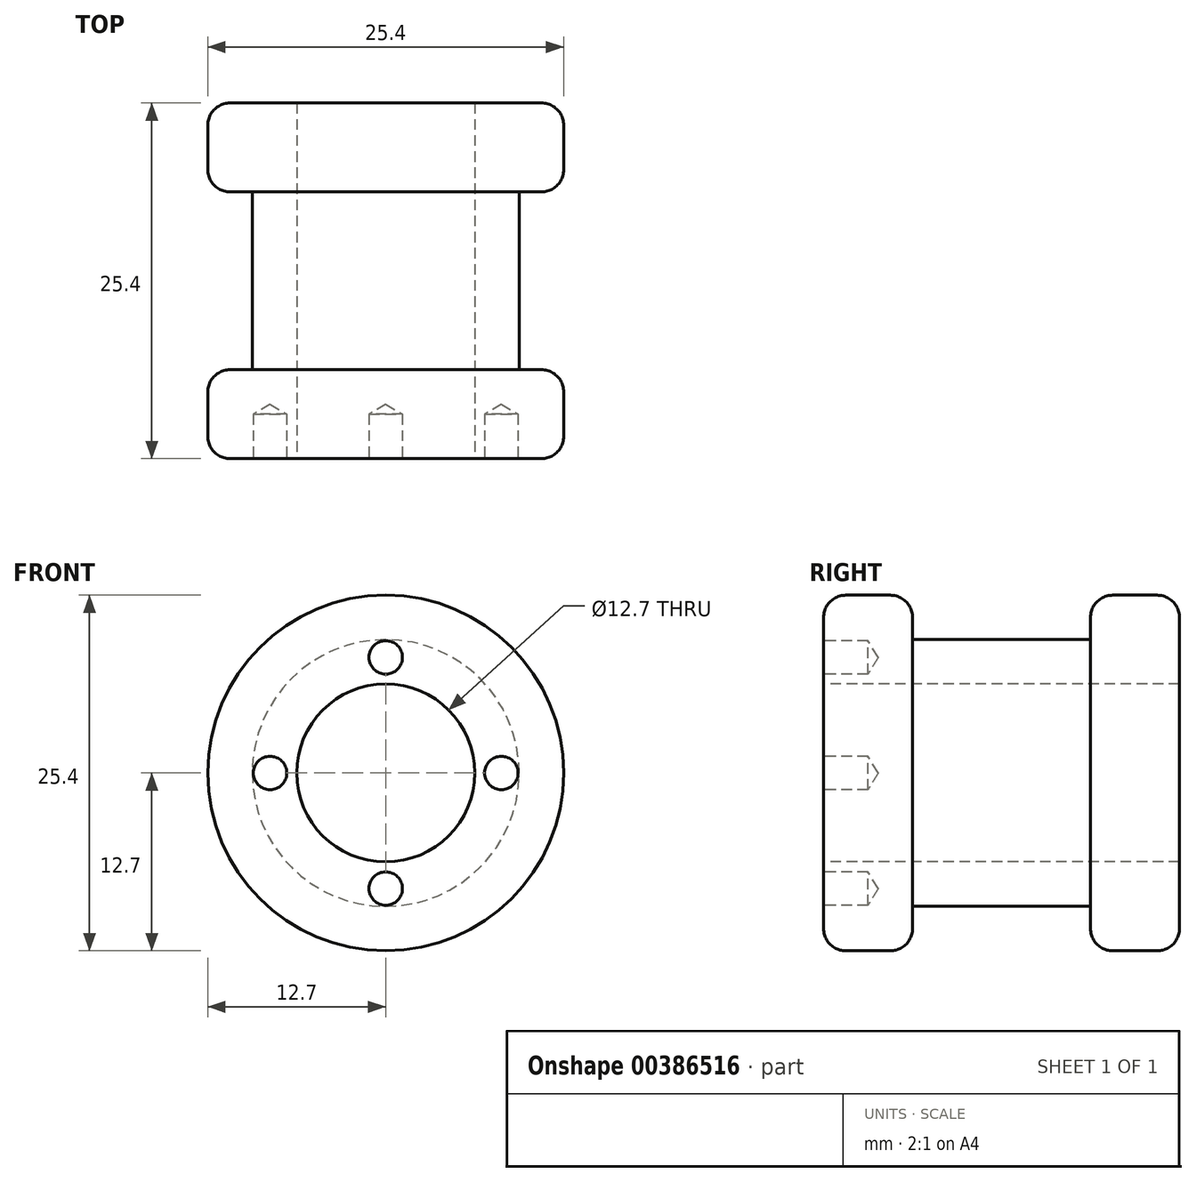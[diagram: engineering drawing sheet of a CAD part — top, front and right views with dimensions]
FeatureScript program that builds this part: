
annotation { "Feature Type Name" : "Feature", "Feature Type Description" : "" }
export const myFeature = defineFeature(function(context is Context, id is Id, definition is map)
    precondition{}
    {
        {
            var Q0;
            Q0=qCreatedBy(makeId("Front.planeOp"),FACE);
            var sketch = newSketch(context, id + "F0", { "sketchPlane" : qUnion([Q0])});
            skCircle(sketch, "E0", {"center": v(0, 0) * mm, "radius": 12.7 * mm});
            skSolve(sketch);
        }
        {
            var Q0;
            Q0=makeQuery(id+"F0.imprint","IMPRINT",FACE,{"disambiguationData":[TD([[makeQuery(id+"F0.imprint","IMPRINT",EDGE,{"derivedFrom":sQuery(id+"F0.wireOp",EDGE,"E0")}),1.0]])]});
            extrude(context, id + "F1", {"entities" : qUnion([Q0]), "depth" : 6.35 * mm});
        }
        {
            var Q0;
            Q0=makeQuery(id+"F1.opExtrude","CAP_FACE",FACE,{"disambiguationData":[OSD([sQuery(id+"F0.wireOp",EDGE,"E0")])],"isStart":false});
            var sketch = newSketch(context, id + "F2", { "sketchPlane" : qUnion([Q0])});
            skCircle(sketch, "E1", {"center": v(0, 0) * mm, "radius": 9.52 * mm});
            skSolve(sketch);
        }
        {
            var Q0;
            Q0=makeQuery(id+"F2.imprint","IMPRINT",FACE,{"disambiguationData":[TD([[makeQuery(id+"F2.imprint","IMPRINT",EDGE,{"derivedFrom":sQuery(id+"F2.wireOp",EDGE,"E1")}),1.0]])]});
            extrude(context, id + "F3", {"entities" : qUnion([Q0]), "operationType" : NewBodyOperationType.ADD, "depth" : 12.7 * mm});
        }
        {
            var Q0;
            Q0=makeQuery(id+"F3.opExtrude","CAP_FACE",FACE,{"disambiguationData":[OSD([sQuery(id+"F2.wireOp",EDGE,"E1")])],"isStart":false});
            var sketch = newSketch(context, id + "F4", { "sketchPlane" : qUnion([Q0])});
            skCircle(sketch, "E2", {"center": v(0, 0) * mm, "radius": 12.7 * mm});
            skSolve(sketch);
        }
        {
            var Q0;
            Q0=makeQuery(id+"F4.imprint","IMPRINT",FACE,{"disambiguationData":[TD([[makeQuery(id+"F4.imprint","IMPRINT",EDGE,{"derivedFrom":sQuery(id+"F4.wireOp",EDGE,"E2")}),1.0]])]});
            var Q1;
            Q1=makeQuery(id+"F4.imprint","IMPRINT",FACE,{"disambiguationData":[TD([[makeQuery(id+"F4.imprint","IMPRINT",EDGE,{"derivedFrom":makeQuery(id+"F3.opExtrude","CAP_EDGE",EDGE,{"disambiguationData":[OSD([sQuery(id+"F2.wireOp",EDGE,"E1")])],"isStart":false})}),1.0]])]});
            extrude(context, id + "F5", {"entities" : qUnion([Q0, Q1]), "operationType" : NewBodyOperationType.ADD, "depth" : 6.35 * mm});
        }
        {
            var Q0;
            Q0=makeQuery(id+"F5.opExtrude","CAP_FACE",FACE,{"disambiguationData":[OSD([sQuery(id+"F4.wireOp",EDGE,"E2")])],"isStart":false});
            var sketch = newSketch(context, id + "F6", { "sketchPlane" : qUnion([Q0])});
            skPoint(sketch, "E3", {"position": v(0, 8.26) * mm});
            skPoint(sketch, "E4", {"position": v(8.26, 0) * mm});
            skPoint(sketch, "E5", {"position": v(0, -8.26) * mm});
            skPoint(sketch, "E6", {"position": v(-8.26, 0) * mm});
            skPoint(sketch, "E7", {"position": v(0, 0) * mm});
            skSolve(sketch);
        }
        {
            var Q0;
            Q0=sQuery(id+"F6.wireOp",VERTEX,"E7");
            var Q1;
            Q1=makeQuery(id+"F1.opExtrude","SWEPT_BODY",BODY,{"disambiguationData":[OSD([sQuery(id+"F0.wireOp",EDGE,"E0")])]});
            hole(context, id + "F7", {"style" : HoleStyle.SIMPLE, "endStyle" : HoleEndStyle.THROUGH, "holeDiameter" : 12.7 * mm, "isTappedThrough" : true, "tappedDepth" : 12.7 * mm, "tapClearance" : 3, "locations" : qUnion([Q0]), "scope" : qUnion([Q1])});
        }
        {
            var Q0;
            Q0=sQuery(id+"F6.wireOp",VERTEX,"E3");
            var Q1;
            Q1=sQuery(id+"F6.wireOp",VERTEX,"E6");
            var Q2;
            Q2=sQuery(id+"F6.wireOp",VERTEX,"E5");
            var Q3;
            Q3=sQuery(id+"F6.wireOp",VERTEX,"E4");
            var Q4;
            Q4=makeQuery(id+"F1.opExtrude","SWEPT_BODY",BODY,{"disambiguationData":[OSD([sQuery(id+"F0.wireOp",EDGE,"E0")])]});
            hole(context, id + "F8", {"style" : HoleStyle.SIMPLE, "endStyle" : HoleEndStyle.BLIND, "holeDiameter" : 2.4 * mm, "holeDepth" : 3.17 * mm, "isTappedThrough" : true, "tappedDepth" : 12.7 * mm, "tapClearance" : 3, "locations" : qUnion([Q0, Q1, Q2, Q3]), "scope" : qUnion([Q4])});
        }
        {
            var Q0;
            Q0=makeQuery(id+"F5.opExtrude","CAP_EDGE",EDGE,{"disambiguationData":[OSD([sQuery(id+"F4.wireOp",EDGE,"E2")])],"isStart":false});
            var Q1;
            Q1=makeQuery(id+"F5.opExtrude","CAP_EDGE",EDGE,{"disambiguationData":[OSD([sQuery(id+"F4.wireOp",EDGE,"E2")])],"isStart":true});
            var Q2;
            Q2=makeQuery(id+"F1.opExtrude","CAP_EDGE",EDGE,{"disambiguationData":[OSD([sQuery(id+"F0.wireOp",EDGE,"E0")])],"isStart":false});
            var Q3;
            Q3=makeQuery(id+"F1.opExtrude","CAP_EDGE",EDGE,{"disambiguationData":[OSD([sQuery(id+"F0.wireOp",EDGE,"E0")])],"isStart":true});
            var Q4;
            Q4=makeQuery(id+"F3.opExtrude","CAP_EDGE",EDGE,{"disambiguationData":[OSD([sQuery(id+"F2.wireOp",EDGE,"E1")])],"isStart":true});
            var Q5;
            Q5=makeQuery(id+"F3.opExtrude","CAP_EDGE",EDGE,{"disambiguationData":[OSD([sQuery(id+"F2.wireOp",EDGE,"E1")])],"isStart":false});
            fillet(context, id + "F9", {"entities" : qUnion([Q0, Q1, Q2, Q3, Q4, Q5]), "radius" : 1.59 * mm, "tangentPropagation" : true, "allowEdgeOverflow" : false});
        }
    });
